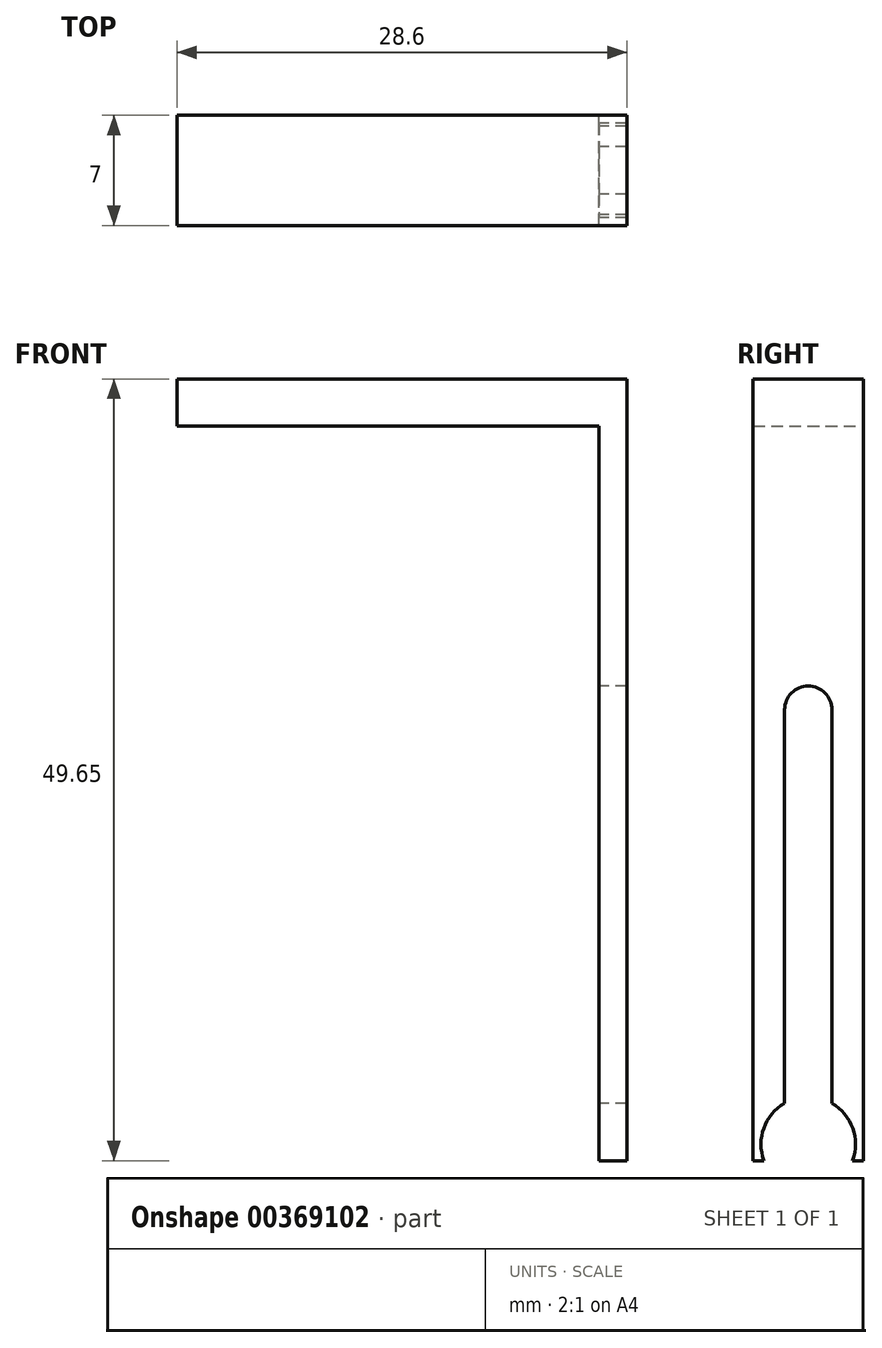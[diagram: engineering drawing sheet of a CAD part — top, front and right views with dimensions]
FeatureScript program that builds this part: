
annotation { "Feature Type Name" : "Feature", "Feature Type Description" : "" }
export const myFeature = defineFeature(function(context is Context, id is Id, definition is map)
    precondition{}
    {
        {
            var Q0;
            Q0=qCreatedBy(makeId("Right.planeOp"),FACE);
            var sketch = newSketch(context, id + "F0", { "sketchPlane" : qUnion([Q0])});
            skLineSegment(sketch, "E0.left", {"start": v(-1.36, 13.78) * mm, "end": v(-1.36, -11.22) * mm});
            skLineSegment(sketch, "E0.right", {"start": v(1.64, 13.78) * mm, "end": v(1.64, -11.22) * mm});
            skArc(sketch, "E1", {"start": v(1.64, 13.78) * mm, "mid": v(0.14, 15.28) * mm, "end": v(-1.36, 13.78) * mm});
            skArc(sketch, "E2", {"start": v(-1.36, -11.22) * mm, "mid": v(-2.68, -12.8) * mm, "end": v(-2.67, -14.87) * mm});
            skLineSegment(sketch, "E3.bottom", {"start": v(-3.36, 34.78) * mm, "end": v(3.64, 34.78) * mm});
            skLineSegment(sketch, "E3.top", {"start": v(-3.36, -14.87) * mm, "end": v(-2.67, -14.87) * mm});
            skLineSegment(sketch, "E3.left", {"start": v(-3.36, 34.78) * mm, "end": v(-3.36, -14.87) * mm});
            skLineSegment(sketch, "E3.right", {"start": v(3.64, 34.78) * mm, "end": v(3.64, -14.87) * mm});
            skLineSegment(sketch, "E4.trimOffspring", {"start": v(2.95, -14.87) * mm, "end": v(3.64, -14.87) * mm});
            skArc(sketch, "E5.trimOffspring", {"start": v(2.95, -14.87) * mm, "mid": v(2.96, -12.8) * mm, "end": v(1.64, -11.22) * mm});
            skSolve(sketch);
        }
        {
            var Q0;
            Q0=makeQuery(id+"F0.imprint","IMPRINT",FACE,{"disambiguationData":[TD([[makeQuery(id+"F0.imprint","IMPRINT",EDGE,{"derivedFrom":sQuery(id+"F0.wireOp",EDGE,"E0.left")}),-1.0]])]});
            var sketch = newSketch(context, id + "F1", { "sketchPlane" : qUnion([Q0])});
            skSolve(sketch);
        }
        {
            var Q0;
            Q0=makeQuery(id+"F0.imprint","IMPRINT",FACE,{"disambiguationData":[TD([[makeQuery(id+"F0.imprint","IMPRINT",EDGE,{"derivedFrom":sQuery(id+"F0.wireOp",EDGE,"E0.left")}),-1.0]])]});
            extrude(context, id + "F2", {"entities" : qUnion([Q0]), "depth" : 1.8 * mm});
        }
        {
            var Q0;
            Q0=makeQuery(id+"F1.imprint","IMPRINT",FACE,{"disambiguationData":[TD([[makeQuery(id+"F1.imprint","IMPRINT",EDGE,{"derivedFrom":makeQuery(id+"F0.imprint","IMPRINT",EDGE,{"derivedFrom":sQuery(id+"F0.wireOp",EDGE,"E0.left")})}),-1.0]])]});
            var sketch = newSketch(context, id + "F3", { "sketchPlane" : qUnion([Q0])});
            skLineSegment(sketch, "E6.bottom", {"start": v(-3.36, 34.78) * mm, "end": v(3.64, 34.78) * mm});
            skLineSegment(sketch, "E6.top", {"start": v(-3.36, 31.78) * mm, "end": v(3.64, 31.78) * mm});
            skLineSegment(sketch, "E6.left", {"start": v(-3.36, 34.78) * mm, "end": v(-3.36, 31.78) * mm});
            skLineSegment(sketch, "E6.right", {"start": v(3.64, 34.78) * mm, "end": v(3.64, 31.78) * mm});
            skSolve(sketch);
        }
        {
            var Q0;
            Q0 = qSketchRegion(id + "F3", true);
            extrude(context, id + "F4", {"entities" : qUnion([Q0]), "operationType" : NewBodyOperationType.ADD, "oppositeDirection" : true, "depth" : 26.8 * mm});
        }
    });
